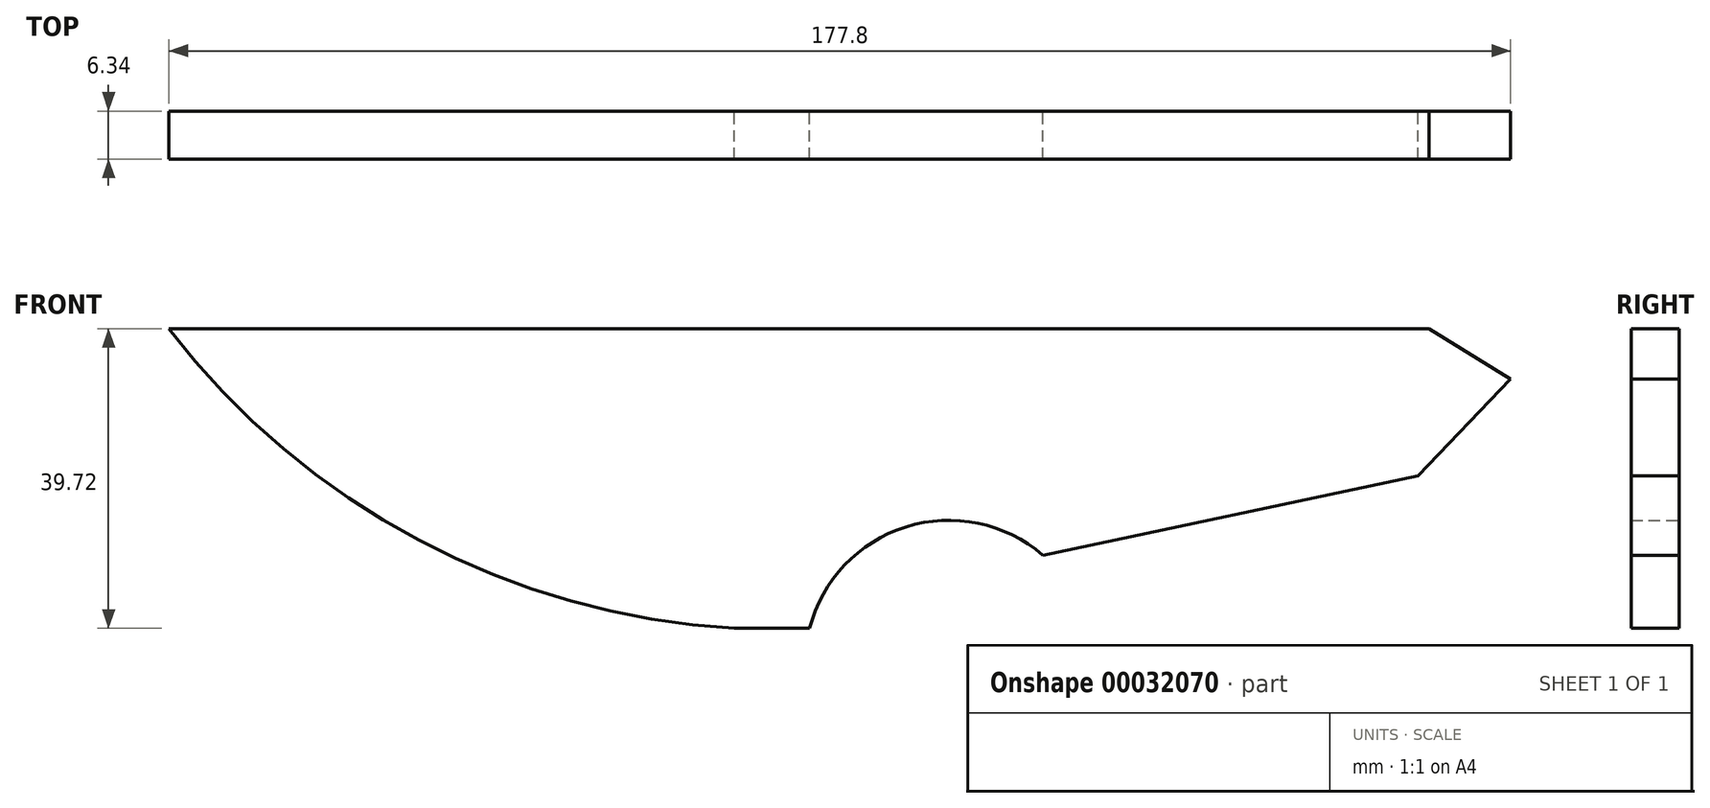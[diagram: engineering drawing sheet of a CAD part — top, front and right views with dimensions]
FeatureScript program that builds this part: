
annotation { "Feature Type Name" : "Feature", "Feature Type Description" : "" }
export const myFeature = defineFeature(function(context is Context, id is Id, definition is map)
    precondition{}
    {
        {
            var Q0;
            Q0=qCreatedBy(makeId("Front.planeOp"),FACE);
            var sketch = newSketch(context, id + "F0", { "sketchPlane" : qUnion([Q0])});
            skLineSegment(sketch, "E0", {"start": v(0, 0) * mm, "end": v(-74.88, 0) * mm});
            skArc(sketch, "E1", {"start": v(-74.88, 0) * mm, "mid": v(-41.78, -28.04) * mm, "end": v(0, -39.72) * mm});
            skLineSegment(sketch, "E2", {"start": v(0, -39.72) * mm, "end": v(10.02, -39.72) * mm});
            skArc(sketch, "E3", {"start": v(40.92, -30.02) * mm, "mid": v(22.77, -26.27) * mm, "end": v(10.02, -39.72) * mm});
            skLineSegment(sketch, "E4", {"start": v(40.92, -30.02) * mm, "end": v(90.62, -19.53) * mm});
            skLineSegment(sketch, "E5", {"start": v(90.62, -19.53) * mm, "end": v(102.92, -6.68) * mm});
            skLineSegment(sketch, "E6", {"start": v(102.92, -6.68) * mm, "end": v(92.12, 0) * mm});
            skLineSegment(sketch, "E7", {"start": v(92.12, 0) * mm, "end": v(0, 0) * mm});
            skSolve(sketch);
        }
        {
            var Q0;
            Q0 = qSketchRegion(id + "F0", true);
            extrude(context, id + "F1", {"entities" : qUnion([Q0]), "endBound" : BoundingType.SYMMETRIC, "depth" : 6.35 * mm});
        }
    });
